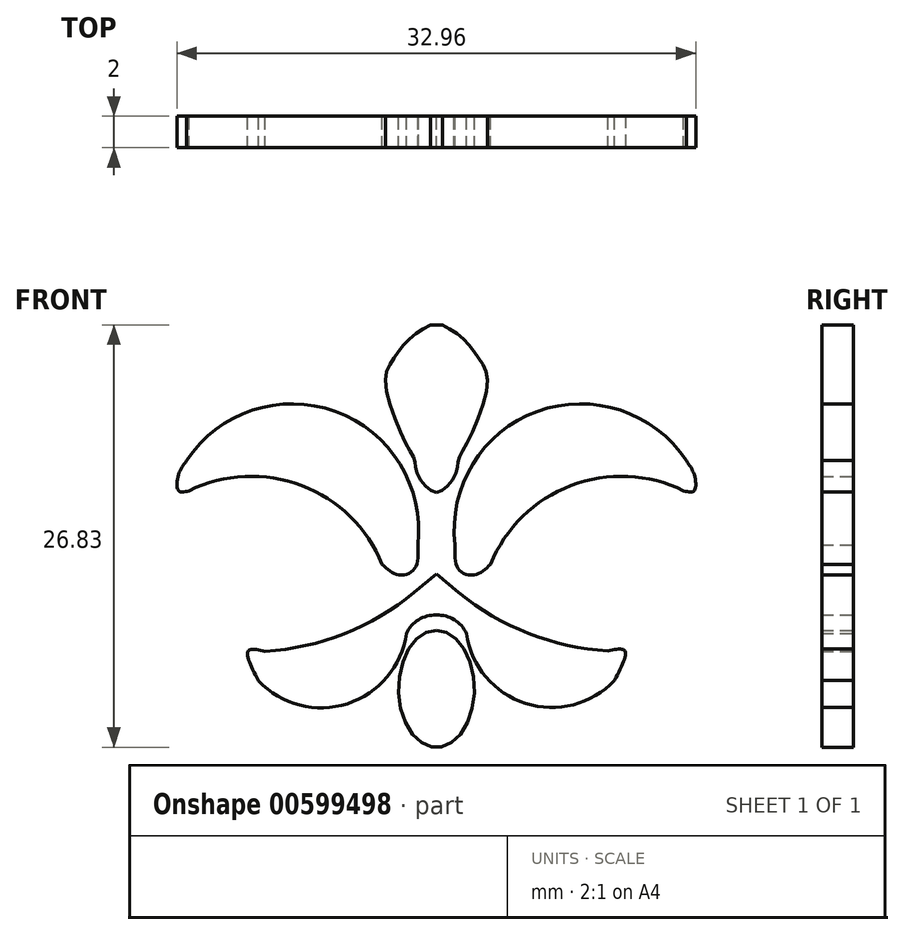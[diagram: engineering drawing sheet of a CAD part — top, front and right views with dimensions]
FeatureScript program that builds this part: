
annotation { "Feature Type Name" : "Feature", "Feature Type Description" : "" }
export const myFeature = defineFeature(function(context is Context, id is Id, definition is map)
    precondition{}
    {
        {
            var Q0;
            Q0=qCreatedBy(makeId("Front.planeOp"),FACE);
            var sketch = newSketch(context, id + "F0", { "sketchPlane" : qUnion([Q0])});
            skArc(sketch, "E0", {"start": v(-5.83, -59.9) * mm, "mid": v(-10.95, -54.9) * mm, "end": v(-18.1, -55.23) * mm});
            skArc(sketch, "E1", {"start": v(-3.57, -58.67) * mm, "mid": v(-8.8, -50.19) * mm, "end": v(-18.26, -53.32) * mm});
            skFitSpline(sketch, "E2", {"points": [v(-18.26, -53.32) * mm, v(-18.79, -54.27) * mm, v(-18.75, -55.23) * mm, v(-18.1, -55.23) * mm], "startDerivative": vector(-1.69, -2.33) * mm, "endDerivative": vector(2.75, 0.69) * mm});
            skFitSpline(sketch, "E3", {"points": [v(-3.57, -58.67) * mm, v(-3.82, -60.25) * mm, v(-4.9, -60.55) * mm, v(-5.83, -59.9) * mm], "startDerivative": vector(0.17, -4.95) * mm, "endDerivative": vector(-2.68, 2.65) * mm});
            skArc(sketch, "E4", {"start": v(-0.97, -61.69) * mm, "mid": v(3.47, -64.3) * mm, "end": v(8.5, -65.4) * mm});
            skArc(sketch, "E5", {"start": v(-0.48, -64.3) * mm, "mid": v(3.28, -68.74) * mm, "end": v(8.91, -67.28) * mm});
            skPoint(sketch, "E5.startSnap0", {"position": v(3.47, -64.3) * mm});
            skFitSpline(sketch, "E6", {"points": [v(8.5, -65.4) * mm, v(9.58, -65.4) * mm, v(8.91, -67.28) * mm], "startDerivative": vector(3.35, 0.7) * mm, "endDerivative": vector(-2.23, -4.21) * mm});
            skArc(sketch, "E7", {"start": v(-0.48, -64.3) * mm, "mid": v(-1.25, -63.42) * mm, "end": v(-2.39, -63.13) * mm});
            skLineSegment(sketch, "E8", {"start": v(-0.97, -61.69) * mm, "end": v(-2.4, -60.52) * mm});
            skArc(sketch, "E9", {"start": v(-10, -47.6) * mm, "mid": v(-15.49, -47.51) * mm, "end": v(-18.72, -51.96) * mm, "construction": true});
            skArc(sketch, "E10", {"start": v(-7.59, -49.88) * mm, "mid": v(-13.52, -48.96) * mm, "end": v(-18.72, -51.96) * mm, "construction": true});
            skLineSegment(sketch, "E11", {"start": v(-10, -47.6) * mm, "end": v(-6.87, -44.7) * mm, "construction": true});
            skLineSegment(sketch, "E12", {"start": v(-6.87, -44.7) * mm, "end": v(-4.86, -44.7) * mm, "construction": true});
            skArc(sketch, "E13", {"start": v(-4.86, -44.7) * mm, "mid": v(-6.94, -46.91) * mm, "end": v(-7.59, -49.88) * mm, "construction": true});
            skFitSpline(sketch, "E14", {"points": [v(-2.76, -44.7) * mm, v(-4.16, -45.64) * mm, v(-5.12, -46.88) * mm, v(-5.64, -48.24) * mm, v(-4.33, -52.21) * mm, v(-3.77, -53.3) * mm, v(-3.67, -54) * mm, v(-2.9, -55.1) * mm, v(-2.14, -55.39) * mm], "startDerivative": vector(-11.31, -6.37) * mm, "endDerivative": vector(8.26, -1.63) * mm});
            skLineSegment(sketch, "E15", {"start": v(-2.76, -44.7) * mm, "end": v(-2.4, -44.7) * mm});
            skEllipse(sketch, "E16", {"center": v(-2.39, -67.8) * mm, "majorRadius": 3.72 * mm, "minorRadius": 2.4 * mm, "majorAxis": v(0, 1)});
            skLineSegment(sketch, "E17", {"start": v(-2.4, -55.34) * mm, "end": v(-2.4, -44.7) * mm});
            skFitSpline(sketch, "E18.MirrorCS", {"points": [v(-2.02, -44.7) * mm, v(-0.62, -45.64) * mm, v(0.34, -46.88) * mm, v(0.86, -48.24) * mm, v(-0.46, -52.21) * mm, v(-1.01, -53.3) * mm, v(-1.11, -54) * mm, v(-1.88, -55.1) * mm, v(-2.64, -55.39) * mm], "startDerivative": vector(11.31, -6.37) * mm, "endDerivative": vector(-8.26, -1.63) * mm});
            skLineSegment(sketch, "E19", {"start": v(-2.4, -44.7) * mm, "end": v(-2.02, -44.7) * mm});
            skArc(sketch, "E20.MirrorCS", {"start": v(5.21, -47.6) * mm, "mid": v(10.7, -47.51) * mm, "end": v(13.94, -51.96) * mm, "construction": true});
            skArc(sketch, "E21.MirrorCS", {"start": v(0.08, -44.7) * mm, "mid": v(2.16, -46.91) * mm, "end": v(2.8, -49.88) * mm, "construction": true});
            skLineSegment(sketch, "E22.MirrorCS", {"start": v(2.09, -44.7) * mm, "end": v(0.08, -44.7) * mm, "construction": true});
            skLineSegment(sketch, "E23.MirrorCS", {"start": v(5.21, -47.6) * mm, "end": v(2.09, -44.7) * mm, "construction": true});
            skArc(sketch, "E24.MirrorCS", {"start": v(2.8, -49.88) * mm, "mid": v(8.74, -48.96) * mm, "end": v(13.94, -51.96) * mm, "construction": true});
            skFitSpline(sketch, "E25.MirrorCS", {"points": [v(13.48, -53.32) * mm, v(14, -54.27) * mm, v(13.97, -55.23) * mm, v(13.31, -55.23) * mm], "startDerivative": vector(1.69, -2.33) * mm, "endDerivative": vector(-2.75, 0.69) * mm});
            skFitSpline(sketch, "E26.MirrorCS", {"points": [v(-1.21, -58.67) * mm, v(-0.96, -60.25) * mm, v(0.11, -60.55) * mm, v(1.05, -59.9) * mm], "startDerivative": vector(-0.17, -4.95) * mm, "endDerivative": vector(2.68, 2.65) * mm});
            skArc(sketch, "E27.MirrorCS", {"start": v(-1.21, -58.67) * mm, "mid": v(4.02, -50.19) * mm, "end": v(13.48, -53.32) * mm});
            skArc(sketch, "E28.MirrorCS", {"start": v(1.05, -59.9) * mm, "mid": v(6.16, -54.9) * mm, "end": v(13.31, -55.23) * mm});
            skArc(sketch, "E29.MirrorCS", {"start": v(-3.8, -61.7) * mm, "mid": v(-8.24, -64.3) * mm, "end": v(-13.27, -65.42) * mm});
            skArc(sketch, "E30.MirrorCS", {"start": v(-4.3, -64.3) * mm, "mid": v(-8.04, -68.75) * mm, "end": v(-13.68, -67.3) * mm});
            skPoint(sketch, "E31.MirrorP", {"position": v(-8.24, -64.3) * mm});
            skFitSpline(sketch, "E32.MirrorCS", {"points": [v(-13.27, -65.42) * mm, v(-14.35, -65.42) * mm, v(-13.68, -67.3) * mm], "startDerivative": vector(-3.35, 0.69) * mm, "endDerivative": vector(2.24, -4.2) * mm});
            skArc(sketch, "E33.MirrorCS", {"start": v(-4.3, -64.3) * mm, "mid": v(-3.52, -63.42) * mm, "end": v(-2.39, -63.13) * mm});
            skLineSegment(sketch, "E34.MirrorCS", {"start": v(-3.8, -61.7) * mm, "end": v(-2.4, -60.52) * mm});
            skSolve(sketch);
        }
        {
            var Q0;
            Q0 = qSketchRegion(id + "F0", true);
            extrude(context, id + "F1", {"entities" : qUnion([Q0]), "depth" : 2 * mm, "offsetDistance" : 25 * mm});
        }
    });
